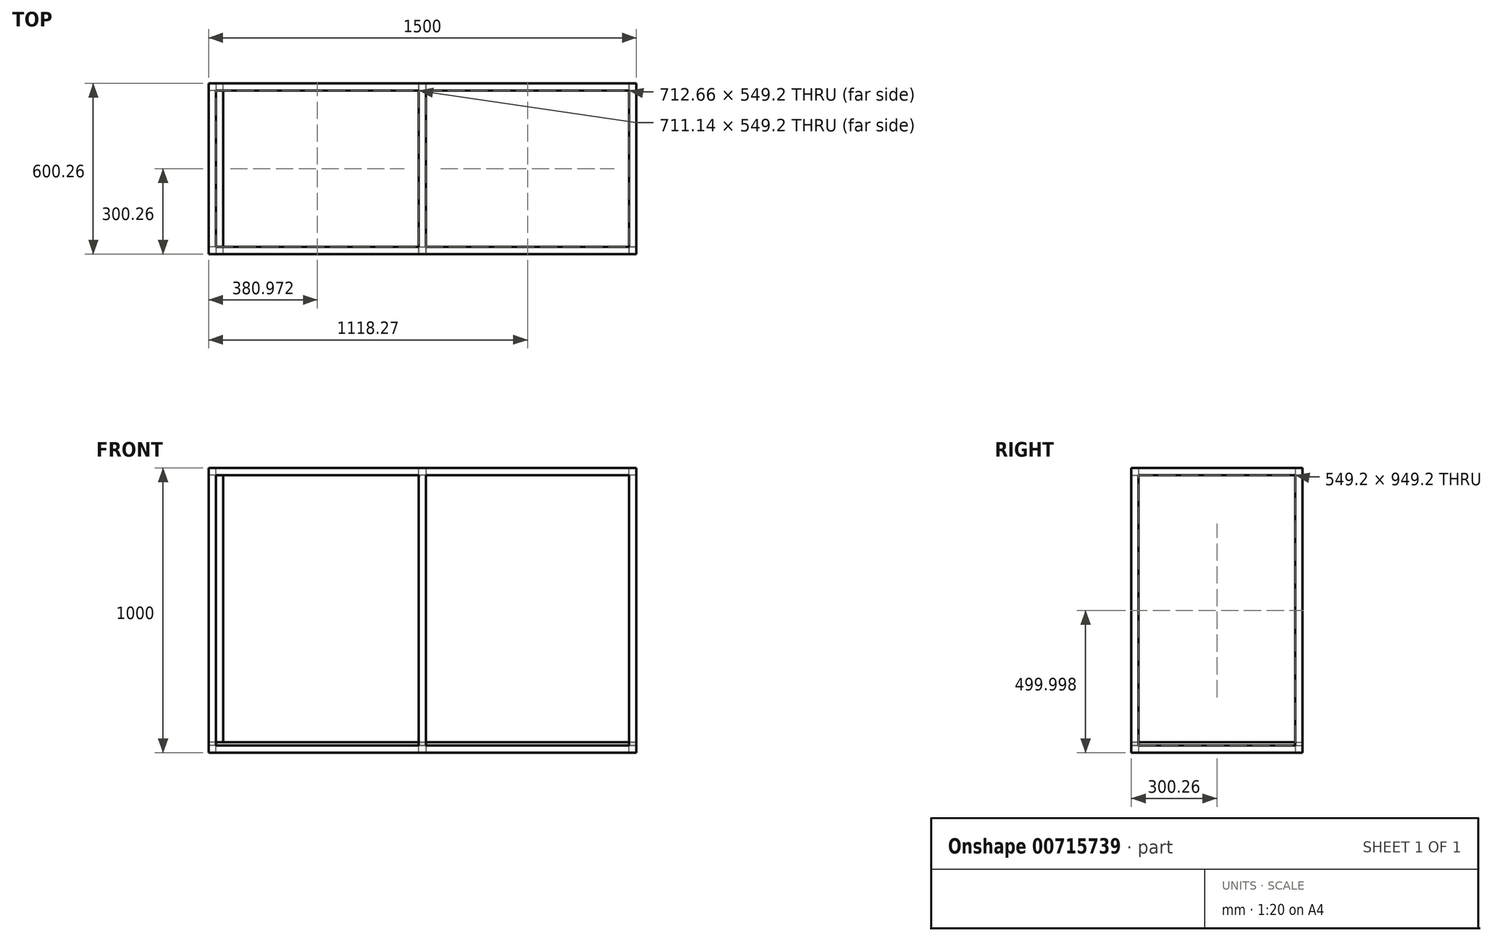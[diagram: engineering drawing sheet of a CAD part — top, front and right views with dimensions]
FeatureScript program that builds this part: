
annotation { "Feature Type Name" : "Feature", "Feature Type Description" : "" }
export const myFeature = defineFeature(function(context is Context, id is Id, definition is map)
    precondition{}
    {
        {
            var Q0;
            Q0=qCreatedBy(makeId("Front.planeOp"),FACE);
            var sketch = newSketch(context, id + "F0", { "sketchPlane" : qUnion([Q0])});
            skLineSegment(sketch, "E0.bottom", {"start": v(-749.24, 203.72) * mm, "end": v(750.76, 203.72) * mm});
            skLineSegment(sketch, "E0.top", {"start": v(-749.24, -796.28) * mm, "end": v(750.76, -796.28) * mm});
            skLineSegment(sketch, "E0.left", {"start": v(-749.24, 203.72) * mm, "end": v(-749.24, -796.28) * mm});
            skLineSegment(sketch, "E0.right", {"start": v(750.76, 203.72) * mm, "end": v(750.76, -796.28) * mm});
            skSolve(sketch);
        }
        {
            var Q0;
            Q0 = qSketchRegion(id + "F0", true);
            extrude(context, id + "F1", {"entities" : qUnion([Q0]), "depth" : 600 * mm, "offsetDistance" : 25 * mm});
        }
        {
            var Q0;
            Q0=makeQuery(id+"F1.opExtrude","CAP_FACE",FACE,{"disambiguationData":[OSD([sQuery(id+"F0.wireOp",EDGE,"E0.bottom"),sQuery(id+"F0.wireOp",EDGE,"E0.top"),sQuery(id+"F0.wireOp",EDGE,"E0.left"),sQuery(id+"F0.wireOp",EDGE,"E0.right")])],"isStart":false});
            var sketch = newSketch(context, id + "F2", { "sketchPlane" : qUnion([Q0])});
            skLineSegment(sketch, "E1.bottom", {"start": v(-723.84, 178.32) * mm, "end": v(725.36, 178.32) * mm});
            skLineSegment(sketch, "E1.top", {"start": v(-723.84, -770.88) * mm, "end": v(725.36, -770.88) * mm});
            skLineSegment(sketch, "E1.left", {"start": v(-723.84, 178.32) * mm, "end": v(-723.84, -770.88) * mm});
            skLineSegment(sketch, "E1.right", {"start": v(725.36, 178.32) * mm, "end": v(725.36, -770.88) * mm});
            skLineSegment(sketch, "E2", {"start": v(13.46, 203.72) * mm, "end": v(13.46, -796.28) * mm});
            skLineSegment(sketch, "E3", {"start": v(-11.94, 203.72) * mm, "end": v(-11.94, -796.28) * mm});
            skLineSegment(sketch, "E4", {"start": v(-11.94, 203.72) * mm, "end": v(13.46, 203.72) * mm});
            skLineSegment(sketch, "E5", {"start": v(-11.94, -796.28) * mm, "end": v(13.46, -796.28) * mm});
            skPoint(sketch, "E6.trimOffspring.end.orphan", {"position": v(0.76, -796.28) * mm});
            skPoint(sketch, "E7.start.orphan", {"position": v(0.76, 203.72) * mm});
            skSolve(sketch);
        }
        {
            var Q0;
            Q0=makeQuery(id+"F2.imprint","IMPRINT",FACE,{"disambiguationData":[TD([[makeQuery(id+"F2.imprint","IMPRINT",EDGE,{"derivedFrom":sQuery(id+"F2.wireOp",EDGE,"E1.bottom")}),-1.0]])]});
            extrude(context, id + "F3", {"entities" : qUnion([Q0]), "operationType" : NewBodyOperationType.REMOVE, "endBound" : BoundingType.THROUGH_ALL, "oppositeDirection" : true, "depth" : 25.4 * mm, "offsetDistance" : 25.4 * mm});
        }
        {
            var Q0;
            Q0=makeQuery(id+"F1.opExtrude","SWEPT_FACE",FACE,{"disambiguationData":[OSD([sQuery(id+"F0.wireOp",EDGE,"E0.left")])]});
            var sketch = newSketch(context, id + "F4", { "sketchPlane" : qUnion([Q0])});
            skLineSegment(sketch, "E8.bottom", {"start": v(25.4, 178.32) * mm, "end": v(574.6, 178.32) * mm});
            skLineSegment(sketch, "E8.top", {"start": v(25.4, -770.88) * mm, "end": v(574.6, -770.88) * mm});
            skLineSegment(sketch, "E8.left", {"start": v(25.4, 178.32) * mm, "end": v(25.4, -770.88) * mm});
            skLineSegment(sketch, "E8.right", {"start": v(574.6, 178.32) * mm, "end": v(574.6, -770.88) * mm});
            skSolve(sketch);
        }
        {
            var Q0;
            Q0=makeQuery(id+"F4.imprint","IMPRINT",FACE,{"disambiguationData":[TD([[makeQuery(id+"F4.imprint","IMPRINT",EDGE,{"derivedFrom":sQuery(id+"F4.wireOp",EDGE,"E8.bottom")}),-1.0]])]});
            extrude(context, id + "F5", {"entities" : qUnion([Q0]), "operationType" : NewBodyOperationType.REMOVE, "endBound" : BoundingType.THROUGH_ALL, "oppositeDirection" : true, "depth" : 25.4 * mm, "offsetDistance" : 25.4 * mm});
        }
        {
            var Q0;
            Q0=makeQuery(id+"F1.opExtrude","SWEPT_FACE",FACE,{"disambiguationData":[OSD([sQuery(id+"F0.wireOp",EDGE,"E0.bottom")])]});
            var sketch = newSketch(context, id + "F6", { "sketchPlane" : qUnion([Q0])});
            skLineSegment(sketch, "E9.bottom", {"start": v(-723.84, -25.4) * mm, "end": v(725.36, -25.4) * mm});
            skLineSegment(sketch, "E9.top", {"start": v(-723.84, -574.6) * mm, "end": v(725.36, -574.6) * mm});
            skLineSegment(sketch, "E9.left", {"start": v(-723.84, -25.4) * mm, "end": v(-723.84, -574.6) * mm});
            skLineSegment(sketch, "E9.right", {"start": v(725.36, -25.4) * mm, "end": v(725.36, -574.6) * mm});
            skSolve(sketch);
        }
        {
            var Q0;
            Q0 = qSketchRegion(id + "F6", true);
            var Q1;
            Q1=makeQuery(id+"F6.imprint","IMPRINT",FACE,{"disambiguationData":[TD([[makeQuery(id+"F6.imprint","IMPRINT",EDGE,{"derivedFrom":sQuery(id+"F6.wireOp",EDGE,"E9.bottom")}),-1.0]])]});
            extrude(context, id + "F7", {"entities" : qUnion([Q0, Q1]), "operationType" : NewBodyOperationType.REMOVE, "endBound" : BoundingType.THROUGH_ALL, "oppositeDirection" : true, "depth" : 25.4 * mm, "offsetDistance" : 25.4 * mm});
        }
        {
            var Q0;
            Q0=makeQuery(id+"F1.opExtrude","CAP_FACE",FACE,{"disambiguationData":[OSD([sQuery(id+"F0.wireOp",EDGE,"E0.bottom"),sQuery(id+"F0.wireOp",EDGE,"E0.top"),sQuery(id+"F0.wireOp",EDGE,"E0.left"),sQuery(id+"F0.wireOp",EDGE,"E0.right")])],"isStart":false});
            var sketch = newSketch(context, id + "F8", { "sketchPlane" : qUnion([Q0])});
            skLineSegment(sketch, "E10", {"start": v(0, 203.72) * mm, "end": v(12.7, 203.72) * mm});
            skLineSegment(sketch, "E11", {"start": v(12.7, 203.72) * mm, "end": v(12.7, -796.28) * mm});
            skLineSegment(sketch, "E12", {"start": v(12.7, -796.28) * mm, "end": v(-12.7, -796.28) * mm});
            skLineSegment(sketch, "E13", {"start": v(-12.7, -796.28) * mm, "end": v(-12.7, 203.72) * mm});
            skLineSegment(sketch, "E14", {"start": v(-12.7, 203.72) * mm, "end": v(0, 203.72) * mm});
            skSolve(sketch);
        }
        {
            var Q0;
            Q0 = qSketchRegion(id + "F8", true);
            extrude(context, id + "F9", {"entities" : qUnion([Q0]), "operationType" : NewBodyOperationType.ADD, "oppositeDirection" : true, "depth" : 599.97 * mm, "offsetDistance" : 25.4 * mm});
        }
        {
            var Q0;
            Q0=makeQuery(id+"F1.opExtrude","SWEPT_FACE",FACE,{"disambiguationData":[OSD([sQuery(id+"F0.wireOp",EDGE,"E0.right")])]});
            var sketch = newSketch(context, id + "F10", { "sketchPlane" : qUnion([Q0])});
            skLineSegment(sketch, "E15.bottom", {"start": v(-574.6, 178.32) * mm, "end": v(-25.4, 178.32) * mm});
            skLineSegment(sketch, "E15.top", {"start": v(-574.6, -770.88) * mm, "end": v(-25.4, -770.88) * mm});
            skLineSegment(sketch, "E15.left", {"start": v(-574.6, 178.32) * mm, "end": v(-574.6, -770.88) * mm});
            skLineSegment(sketch, "E15.right", {"start": v(-25.4, 178.32) * mm, "end": v(-25.4, -770.88) * mm});
            skSolve(sketch);
        }
        {
            var Q0;
            Q0 = qSketchRegion(id + "F10", true);
            extrude(context, id + "F11", {"entities" : qUnion([Q0]), "operationType" : NewBodyOperationType.REMOVE, "endBound" : BoundingType.THROUGH_ALL, "oppositeDirection" : true, "depth" : 25.4 * mm, "offsetDistance" : 25.4 * mm});
        }
        {
            var Q0;
            {var subQ1=makeQuery(id+"F3.boolean.opBoolean","COPY",FACE,{"derivedFrom":makeQuery(id+"F3.opExtrude","SWEPT_FACE",FACE,{"disambiguationData":[OSD([sQuery(id+"F2.wireOp",EDGE,"E1.top")])]})});var subQ4=makeQuery(id+"F1.opExtrude","SWEPT_FACE",FACE,{"disambiguationData":[OSD([sQuery(id+"F0.wireOp",EDGE,"E0.left")])]});var subQ5=makeQuery(id+"F5.opExtrude","SWEPT_FACE",FACE,{"disambiguationData":[OSD([sQuery(id+"F4.wireOp",EDGE,"E8.top")])]});Q0=makeQuery(id+"F7.boolean.opBoolean","SPLIT",FACE,{"disambiguationData":[TD([subQ4])],"derivedFrom":makeQuery(id+"F5.boolean.opBoolean","MERGE",FACE,{"derivedFrom":[subQ1,subQ5]})});}
            var sketch = newSketch(context, id + "F12", { "sketchPlane" : qUnion([Q0])});
            skLineSegment(sketch, "E16", {"start": v(-749.24, -574.6) * mm, "end": v(-723.84, -574.6) * mm});
            skLineSegment(sketch, "E17", {"start": v(-723.84, -574.6) * mm, "end": v(-723.84, -600.26) * mm});
            skLineSegment(sketch, "E18", {"start": v(-723.84, -600.26) * mm, "end": v(-12.85, -600.26) * mm});
            skLineSegment(sketch, "E19", {"start": v(-12.85, -600.26) * mm, "end": v(-12.85, -574.6) * mm});
            skLineSegment(sketch, "E20", {"start": v(-12.85, -574.6) * mm, "end": v(12.71, -574.6) * mm});
            skLineSegment(sketch, "E21", {"start": v(12.71, -574.6) * mm, "end": v(12.71, -600.26) * mm});
            skLineSegment(sketch, "E22", {"start": v(12.71, -600.26) * mm, "end": v(725.1, -600.26) * mm});
            skLineSegment(sketch, "E23", {"start": v(725.1, -600.26) * mm, "end": v(725.1, -574.6) * mm});
            skLineSegment(sketch, "E24", {"start": v(725.1, -574.6) * mm, "end": v(750.71, -574.6) * mm});
            skLineSegment(sketch, "E25", {"start": v(750.71, -574.6) * mm, "end": v(750.71, -25.4) * mm});
            skLineSegment(sketch, "E26", {"start": v(750.71, -25.4) * mm, "end": v(725.1, -25.4) * mm});
            skLineSegment(sketch, "E27", {"start": v(725.1, -25.4) * mm, "end": v(725.1, 0) * mm});
            skLineSegment(sketch, "E28", {"start": v(725.1, 0) * mm, "end": v(12.71, 0) * mm});
            skLineSegment(sketch, "E29", {"start": v(12.71, 0) * mm, "end": v(12.71, -25.4) * mm});
            skLineSegment(sketch, "E30", {"start": v(12.71, -25.4) * mm, "end": v(-12.85, -25.4) * mm});
            skLineSegment(sketch, "E31", {"start": v(-12.85, -25.4) * mm, "end": v(-12.85, 0) * mm});
            skLineSegment(sketch, "E32", {"start": v(-12.85, 0) * mm, "end": v(-723.84, 0) * mm});
            skLineSegment(sketch, "E33", {"start": v(-723.84, 0) * mm, "end": v(-723.84, -25.4) * mm});
            skLineSegment(sketch, "E34", {"start": v(-723.84, -25.4) * mm, "end": v(-749.24, -25.4) * mm});
            skLineSegment(sketch, "E35", {"start": v(-749.24, -25.4) * mm, "end": v(-749.24, -574.6) * mm});
            skSolve(sketch);
        }
        {
            var Q0;
            Q0 = qSketchRegion(id + "F12", true);
            extrude(context, id + "F13", {"entities" : qUnion([Q0]), "depth" : 12 * mm, "offsetDistance" : 25.4 * mm});
        }
        {
            var Q0;
            Q0=makeQuery(id+"F5.boolean.opBoolean","SPLIT",FACE,{"disambiguationData":[TD([makeQuery(id+"F5.opExtrude","SWEPT_FACE",FACE,{"disambiguationData":[OSD([sQuery(id+"F4.wireOp",EDGE,"E8.right")])]})])],"derivedFrom":makeQuery(id+"F3.boolean.opBoolean","COPY",FACE,{"derivedFrom":makeQuery(id+"F3.opExtrude","SWEPT_FACE",FACE,{"disambiguationData":[OSD([sQuery(id+"F2.wireOp",EDGE,"E1.left")])]})})});
            var sketch = newSketch(context, id + "F14", { "sketchPlane" : qUnion([Q0])});
            skLineSegment(sketch, "E36.bottom", {"start": v(-600, -759.43) * mm, "end": v(0, -759.43) * mm});
            skLineSegment(sketch, "E36.top", {"start": v(-600, 178.32) * mm, "end": v(0, 178.32) * mm});
            skLineSegment(sketch, "E36.left", {"start": v(-600, -759.43) * mm, "end": v(-600, 178.32) * mm});
            skLineSegment(sketch, "E36.right", {"start": v(0, -759.43) * mm, "end": v(0, 178.32) * mm});
            skSolve(sketch);
        }
        {
            var Q0;
            Q0 = qSketchRegion(id + "F14", true);
            extrude(context, id + "F15", {"entities" : qUnion([Q0]), "depth" : 25.4 * mm, "offsetDistance" : 25.4 * mm});
        }
    });
